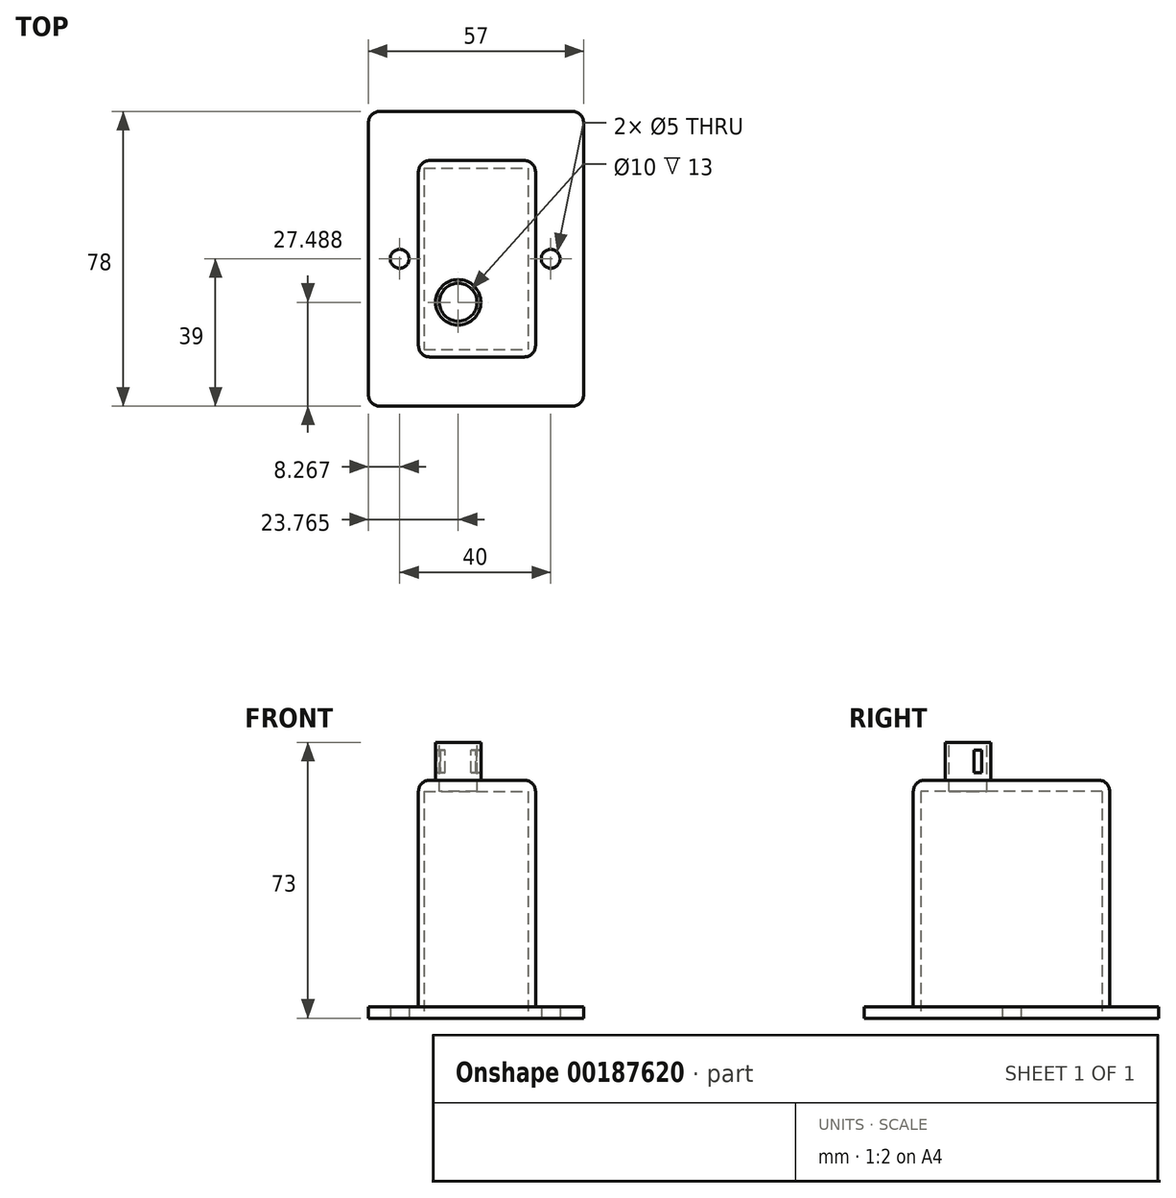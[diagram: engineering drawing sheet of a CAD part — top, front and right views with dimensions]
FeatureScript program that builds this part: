
annotation { "Feature Type Name" : "Feature", "Feature Type Description" : "" }
export const myFeature = defineFeature(function(context is Context, id is Id, definition is map)
    precondition{}
    {
        {
            var Q0;
            Q0=qCreatedBy(makeId("Top.planeOp"),FACE);
            var sketch = newSketch(context, id + "F0", { "sketchPlane" : qUnion([Q0])});
            skLineSegment(sketch, "E0.bottom", {"start": v(-13.75, 24) * mm, "end": v(13.75, 24) * mm});
            skLineSegment(sketch, "E0.top", {"start": v(-13.75, -24) * mm, "end": v(13.75, -24) * mm});
            skLineSegment(sketch, "E0.left", {"start": v(-13.75, 24) * mm, "end": v(-13.75, -24) * mm});
            skLineSegment(sketch, "E0.right", {"start": v(13.75, 24) * mm, "end": v(13.75, -24) * mm});
            skLineSegment(sketch, "E1.bottom", {"start": v(-28.5, 39) * mm, "end": v(28.5, 39) * mm});
            skLineSegment(sketch, "E1.top", {"start": v(-28.5, -39) * mm, "end": v(28.5, -39) * mm});
            skLineSegment(sketch, "E1.left", {"start": v(-28.5, 39) * mm, "end": v(-28.5, -39) * mm});
            skLineSegment(sketch, "E1.right", {"start": v(28.5, 39) * mm, "end": v(28.5, -39) * mm});
            skLineSegment(sketch, "E2.bottom", {"start": v(-15.25, 26) * mm, "end": v(15.75, 26) * mm});
            skLineSegment(sketch, "E2.top", {"start": v(-15.25, -26) * mm, "end": v(15.75, -26) * mm});
            skLineSegment(sketch, "E2.left", {"start": v(-15.25, 26) * mm, "end": v(-15.25, -26) * mm});
            skLineSegment(sketch, "E2.right", {"start": v(15.75, 26) * mm, "end": v(15.75, -26) * mm});
            skSolve(sketch);
        }
        {
            var Q0;
            Q0=makeQuery(id+"F0.imprint","IMPRINT",FACE,{"disambiguationData":[TD([[makeQuery(id+"F0.imprint","IMPRINT",EDGE,{"derivedFrom":sQuery(id+"F0.wireOp",EDGE,"E0.bottom")}),1.0]])]});
            extrude(context, id + "F1", {"entities" : qUnion([Q0]), "depth" : 60 * mm});
        }
        {
            var Q0;
            Q0=makeQuery(id+"F0.imprint","IMPRINT",FACE,{"disambiguationData":[TD([[makeQuery(id+"F0.imprint","IMPRINT",EDGE,{"derivedFrom":sQuery(id+"F0.wireOp",EDGE,"E1.bottom")}),-1.0]])]});
            extrude(context, id + "F2", {"entities" : qUnion([Q0]), "operationType" : NewBodyOperationType.ADD, "depth" : 3 * mm});
        }
        {
            var Q0;
            Q0=makeQuery(id+"F1.opExtrude","CAP_FACE",FACE,{"disambiguationData":[OSD([sQuery(id+"F0.wireOp",EDGE,"E0.bottom"),sQuery(id+"F0.wireOp",EDGE,"E0.top"),sQuery(id+"F0.wireOp",EDGE,"E0.left"),sQuery(id+"F0.wireOp",EDGE,"E0.right"),sQuery(id+"F0.wireOp",EDGE,"E2.bottom"),sQuery(id+"F0.wireOp",EDGE,"E2.top"),sQuery(id+"F0.wireOp",EDGE,"E2.left"),sQuery(id+"F0.wireOp",EDGE,"E2.right")])],"isStart":false});
            var sketch = newSketch(context, id + "F3", { "sketchPlane" : qUnion([Q0])});
            skLineSegment(sketch, "E3.bottom", {"start": v(-15.25, 26) * mm, "end": v(15.75, 26) * mm});
            skLineSegment(sketch, "E3.top", {"start": v(-15.25, -26) * mm, "end": v(15.75, -26) * mm});
            skLineSegment(sketch, "E3.left", {"start": v(-15.25, 26) * mm, "end": v(-15.25, -26) * mm});
            skLineSegment(sketch, "E3.right", {"start": v(15.75, 26) * mm, "end": v(15.75, -26) * mm});
            skSolve(sketch);
        }
        {
            var Q0;
            Q0=makeQuery(id+"F3.imprint","IMPRINT",FACE,{"disambiguationData":[TD([[makeQuery(id+"F3.imprint","IMPRINT",EDGE,{"derivedFrom":sQuery(id+"F3.wireOp",EDGE,"E3.bottom")}),-1.0]])]});
            var Q1;
            Q1=makeQuery(id+"F3.imprint","IMPRINT",FACE,{"disambiguationData":[TD([[makeQuery(id+"F3.imprint","IMPRINT",EDGE,{"derivedFrom":makeQuery(id+"F1.opExtrude","CAP_EDGE",EDGE,{"disambiguationData":[OSD([sQuery(id+"F0.wireOp",EDGE,"E0.bottom")])],"isStart":false})}),-1.0]])]});
            extrude(context, id + "F4", {"entities" : qUnion([Q0, Q1]), "operationType" : NewBodyOperationType.ADD, "depth" : 3 * mm});
        }
        {
            var Q0;
            Q0=makeQuery(id+"F4.opExtrude","CAP_FACE",FACE,{"disambiguationData":[OSD([sQuery(id+"F3.wireOp",EDGE,"E3.bottom"),sQuery(id+"F3.wireOp",EDGE,"E3.top"),sQuery(id+"F3.wireOp",EDGE,"E3.left"),sQuery(id+"F3.wireOp",EDGE,"E3.right")])],"isStart":false});
            var sketch = newSketch(context, id + "F5", { "sketchPlane" : qUnion([Q0])});
            skCircle(sketch, "E4", {"center": v(-4.73, -11.51) * mm, "radius": 5 * mm});
            skCircle(sketch, "E5", {"center": v(-4.73, -11.51) * mm, "radius": 6 * mm});
            skSolve(sketch);
        }
        {
            var Q0;
            Q0=makeQuery(id+"F5.imprint","IMPRINT",FACE,{"disambiguationData":[TD([[makeQuery(id+"F5.imprint","IMPRINT",EDGE,{"derivedFrom":sQuery(id+"F5.wireOp",EDGE,"E4")}),1.0]])]});
            extrude(context, id + "F6", {"entities" : qUnion([Q0]), "operationType" : NewBodyOperationType.REMOVE, "oppositeDirection" : true, "depth" : 4 * mm});
        }
        {
            var Q0;
            Q0=makeQuery(id+"F5.imprint","IMPRINT",FACE,{"disambiguationData":[TD([[makeQuery(id+"F5.imprint","IMPRINT",EDGE,{"derivedFrom":sQuery(id+"F5.wireOp",EDGE,"E4")}),-1.0]])]});
            extrude(context, id + "F7", {"entities" : qUnion([Q0]), "operationType" : NewBodyOperationType.ADD, "depth" : 10 * mm});
        }
        {
            var Q0;
            Q0=makeQuery(id+"F0.imprint","IMPRINT",FACE,{"disambiguationData":[TD([[makeQuery(id+"F0.imprint","IMPRINT",EDGE,{"derivedFrom":sQuery(id+"F0.wireOp",EDGE,"E1.bottom")}),-1.0]])]});
            var sketch = newSketch(context, id + "F8", { "sketchPlane" : qUnion([Q0])});
            skCircle(sketch, "E6", {"center": v(-20.23, 0) * mm, "radius": 2.5 * mm});
            skCircle(sketch, "E7", {"center": v(19.77, 0) * mm, "radius": 2.5 * mm});
            skSolve(sketch);
        }
        {
            var Q0;
            Q0=makeQuery(id+"F8.imprint","IMPRINT",FACE,{"disambiguationData":[TD([[makeQuery(id+"F8.imprint","IMPRINT",EDGE,{"derivedFrom":sQuery(id+"F8.wireOp",EDGE,"E6")}),1.0]])]});
            var Q1;
            Q1=makeQuery(id+"F8.imprint","IMPRINT",FACE,{"disambiguationData":[TD([[makeQuery(id+"F8.imprint","IMPRINT",EDGE,{"derivedFrom":sQuery(id+"F8.wireOp",EDGE,"E7")}),1.0]])]});
            extrude(context, id + "F9", {"entities" : qUnion([Q0, Q1]), "operationType" : NewBodyOperationType.REMOVE, "depth" : 5 * mm});
        }
        {
            var Q0;
            Q0=makeQuery(id+"F2.opExtrude","SWEPT_EDGE",EDGE,{"disambiguationData":[OSD([sQuery(id+"F0.wireOp",EDGE,"E1.bottom"),sQuery(id+"F0.wireOp",EDGE,"E1.right")])]});
            var Q1;
            Q1=makeQuery(id+"F2.opExtrude","SWEPT_EDGE",EDGE,{"disambiguationData":[OSD([sQuery(id+"F0.wireOp",EDGE,"E1.top"),sQuery(id+"F0.wireOp",EDGE,"E1.right")])]});
            var Q2;
            Q2=makeQuery(id+"F2.opExtrude","SWEPT_EDGE",EDGE,{"disambiguationData":[OSD([sQuery(id+"F0.wireOp",EDGE,"E1.bottom"),sQuery(id+"F0.wireOp",EDGE,"E1.left")])]});
            var Q3;
            Q3=makeQuery(id+"F2.opExtrude","SWEPT_EDGE",EDGE,{"disambiguationData":[OSD([sQuery(id+"F0.wireOp",EDGE,"E1.top"),sQuery(id+"F0.wireOp",EDGE,"E1.left")])]});
            var Q4;
            Q4=makeQuery(id+"F4.boolean.opBoolean","MERGE",EDGE,{"derivedFrom":[makeQuery(id+"F1.opExtrude","SWEPT_EDGE",EDGE,{"disambiguationData":[OSD([sQuery(id+"F0.wireOp",EDGE,"E2.bottom"),sQuery(id+"F0.wireOp",EDGE,"E2.left")])]}),makeQuery(id+"F4.opExtrude","SWEPT_EDGE",EDGE,{"disambiguationData":[OSD([sQuery(id+"F3.wireOp",EDGE,"E3.bottom"),sQuery(id+"F3.wireOp",EDGE,"E3.left")])]})]});
            var Q5;
            Q5=makeQuery(id+"F4.boolean.opBoolean","MERGE",EDGE,{"derivedFrom":[makeQuery(id+"F1.opExtrude","SWEPT_EDGE",EDGE,{"disambiguationData":[OSD([sQuery(id+"F0.wireOp",EDGE,"E2.bottom"),sQuery(id+"F0.wireOp",EDGE,"E2.right")])]}),makeQuery(id+"F4.opExtrude","SWEPT_EDGE",EDGE,{"disambiguationData":[OSD([sQuery(id+"F3.wireOp",EDGE,"E3.bottom"),sQuery(id+"F3.wireOp",EDGE,"E3.right")])]})]});
            var Q6;
            Q6=makeQuery(id+"F4.boolean.opBoolean","MERGE",EDGE,{"derivedFrom":[makeQuery(id+"F1.opExtrude","SWEPT_EDGE",EDGE,{"disambiguationData":[OSD([sQuery(id+"F0.wireOp",EDGE,"E2.top"),sQuery(id+"F0.wireOp",EDGE,"E2.left")])]}),makeQuery(id+"F4.opExtrude","SWEPT_EDGE",EDGE,{"disambiguationData":[OSD([sQuery(id+"F3.wireOp",EDGE,"E3.top"),sQuery(id+"F3.wireOp",EDGE,"E3.left")])]})]});
            var Q7;
            Q7=makeQuery(id+"F4.boolean.opBoolean","MERGE",EDGE,{"derivedFrom":[makeQuery(id+"F1.opExtrude","SWEPT_EDGE",EDGE,{"disambiguationData":[OSD([sQuery(id+"F0.wireOp",EDGE,"E2.top"),sQuery(id+"F0.wireOp",EDGE,"E2.right")])]}),makeQuery(id+"F4.opExtrude","SWEPT_EDGE",EDGE,{"disambiguationData":[OSD([sQuery(id+"F3.wireOp",EDGE,"E3.top"),sQuery(id+"F3.wireOp",EDGE,"E3.right")])]})]});
            var Q8;
            Q8=makeQuery(id+"F4.opExtrude","CAP_EDGE",EDGE,{"disambiguationData":[OSD([sQuery(id+"F3.wireOp",EDGE,"E3.right")])],"isStart":false});
            var Q9;
            Q9=makeQuery(id+"F4.opExtrude","CAP_EDGE",EDGE,{"disambiguationData":[OSD([sQuery(id+"F3.wireOp",EDGE,"E3.bottom")])],"isStart":false});
            var Q10;
            Q10=makeQuery(id+"F4.opExtrude","CAP_EDGE",EDGE,{"disambiguationData":[OSD([sQuery(id+"F3.wireOp",EDGE,"E3.left")])],"isStart":false});
            var Q11;
            Q11=makeQuery(id+"F4.opExtrude","CAP_EDGE",EDGE,{"disambiguationData":[OSD([sQuery(id+"F3.wireOp",EDGE,"E3.top")])],"isStart":false});
            fillet(context, id + "F10", {"entities" : qUnion([Q0, Q1, Q2, Q3, Q4, Q5, Q6, Q7, Q8, Q9, Q10, Q11]), "radius" : 3 * mm, "tangentPropagation" : true, "allowEdgeOverflow" : false});
        }
        {
            var Q0;
            Q0=qCreatedBy(makeId("Right.planeOp"),FACE);
            var sketch = newSketch(context, id + "F11", { "sketchPlane" : qUnion([Q0])});
            skLineSegment(sketch, "E8.bottom", {"start": v(-7.87, 71) * mm, "end": v(-9.87, 71) * mm});
            skLineSegment(sketch, "E8.top", {"start": v(-7.87, 65) * mm, "end": v(-9.87, 65) * mm});
            skLineSegment(sketch, "E8.left", {"start": v(-7.87, 71) * mm, "end": v(-7.87, 65) * mm});
            skLineSegment(sketch, "E8.right", {"start": v(-9.87, 71) * mm, "end": v(-9.87, 65) * mm});
            skSolve(sketch);
        }
        {
            var Q0;
            Q0=makeQuery(id+"F11.imprint","IMPRINT",FACE,{"disambiguationData":[TD([[makeQuery(id+"F11.imprint","IMPRINT",EDGE,{"derivedFrom":sQuery(id+"F11.wireOp",EDGE,"E8.bottom")}),1.0]])]});
            extrude(context, id + "F12", {"entities" : qUnion([Q0]), "operationType" : NewBodyOperationType.REMOVE, "oppositeDirection" : true, "depth" : 15 * mm, "hasSecondDirection" : true, "secondDirectionOppositeDirection" : false, "secondDirectionDepth" : 15 * mm});
        }
    });
